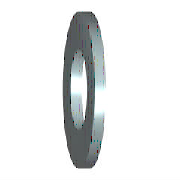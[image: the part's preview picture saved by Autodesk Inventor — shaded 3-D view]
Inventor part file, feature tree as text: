
AUTODESK INVENTOR PART (.ipt)
format: ipt  version: 2024 (Build 280153000, 153)  size: 104,960 bytes
history: native  units: mm (DEFAULTED — no unit token found)
features: other x1, plane x1, sketch x1
ambient origin geometry x7: Origin, YZ Plane, XY Plane, X Axis, Y Axis, Z Axis, Center Point
bodies: Solid1 (feature_tree), Body (feature_tree)
feature tree (3):
  other  "Work Axis1"
  plane  "Work Plane1"
  sketch  "Sketch"  dims[d0=3.2mm d1=7.0mm d2=0.5mm d3=0.0mm d4=0.0mm d5=0.0mm d6=0.0mm d7=0.0mm]
